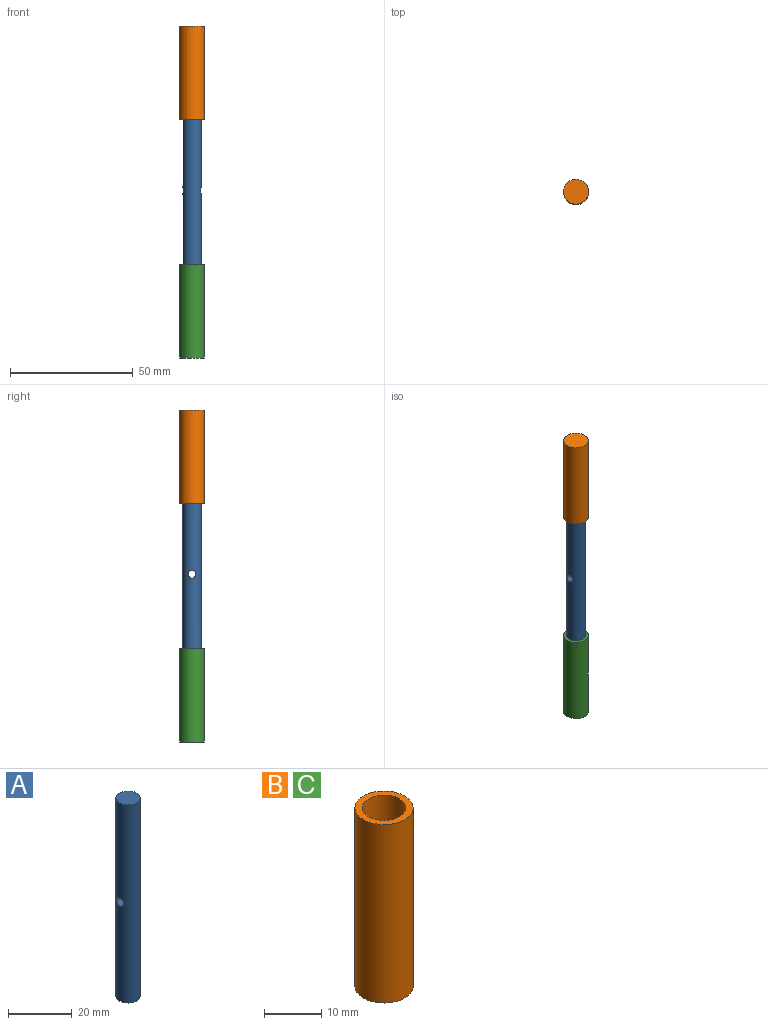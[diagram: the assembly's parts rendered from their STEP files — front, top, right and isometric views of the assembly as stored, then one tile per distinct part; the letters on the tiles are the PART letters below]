
ASSEMBLY  parts=3 mates=2
PART A: 4 faces, bbox 7.6x7.6x76.2 mm
  f0: cylinder r=3.81mm len=76.2mm, axis (0,0,-1), area 1807.9mm2, adj f1,f2,f3
  f1: plane 7.62x7.62mm, normal (0,0,1), area 45.6mm2, adj f0
  f2: plane 7.62x7.62mm, normal (0,0,-1), area 45.6mm2, adj f0
  f3: cylinder r=1.59mm len=7.62mm, axis (1,0,0), area 72.6mm2, adj f0
PART B: 5 faces, bbox 10.2x10.2x38.1 mm
  f0: cylinder r=5.08mm len=38.1mm, axis (0,0,-1), area 1216.1mm2, adj f1,f2
  f1: plane 10.16x10.16mm, normal (0,0,1), area 35.5mm2, adj f0,f3
  f2: plane 10.16x10.16mm, normal (0,0,-1), area 81.1mm2, adj f0
  f3: cylinder r=3.81mm len=31.75mm, axis (0,0,1), area 760.1mm2, adj f1,f4
  f4: plane 7.62x7.62mm, normal (0,0,1), area 45.6mm2, adj f3
PART C: same geometry as B
PLACE A t=(-7.25,-12.32,-14.02)mm
PLACE B rot(axis=(-0.61,-0.79,0),180deg) t=(-7.25,-12.32,91.09)mm
PLACE C rot(axis=(0,0,-1),56deg) t=(-7.25,-12.32,-44.29)mm
MATE cylindrical A.f0 <-> B.f3  axis (0,0,-1) through (-7.25,-12.32,62.18)mm
MATE cylindrical A.f0 <-> C.f3  axis (0,0,-1) through (-7.25,-12.32,24.08)mm
